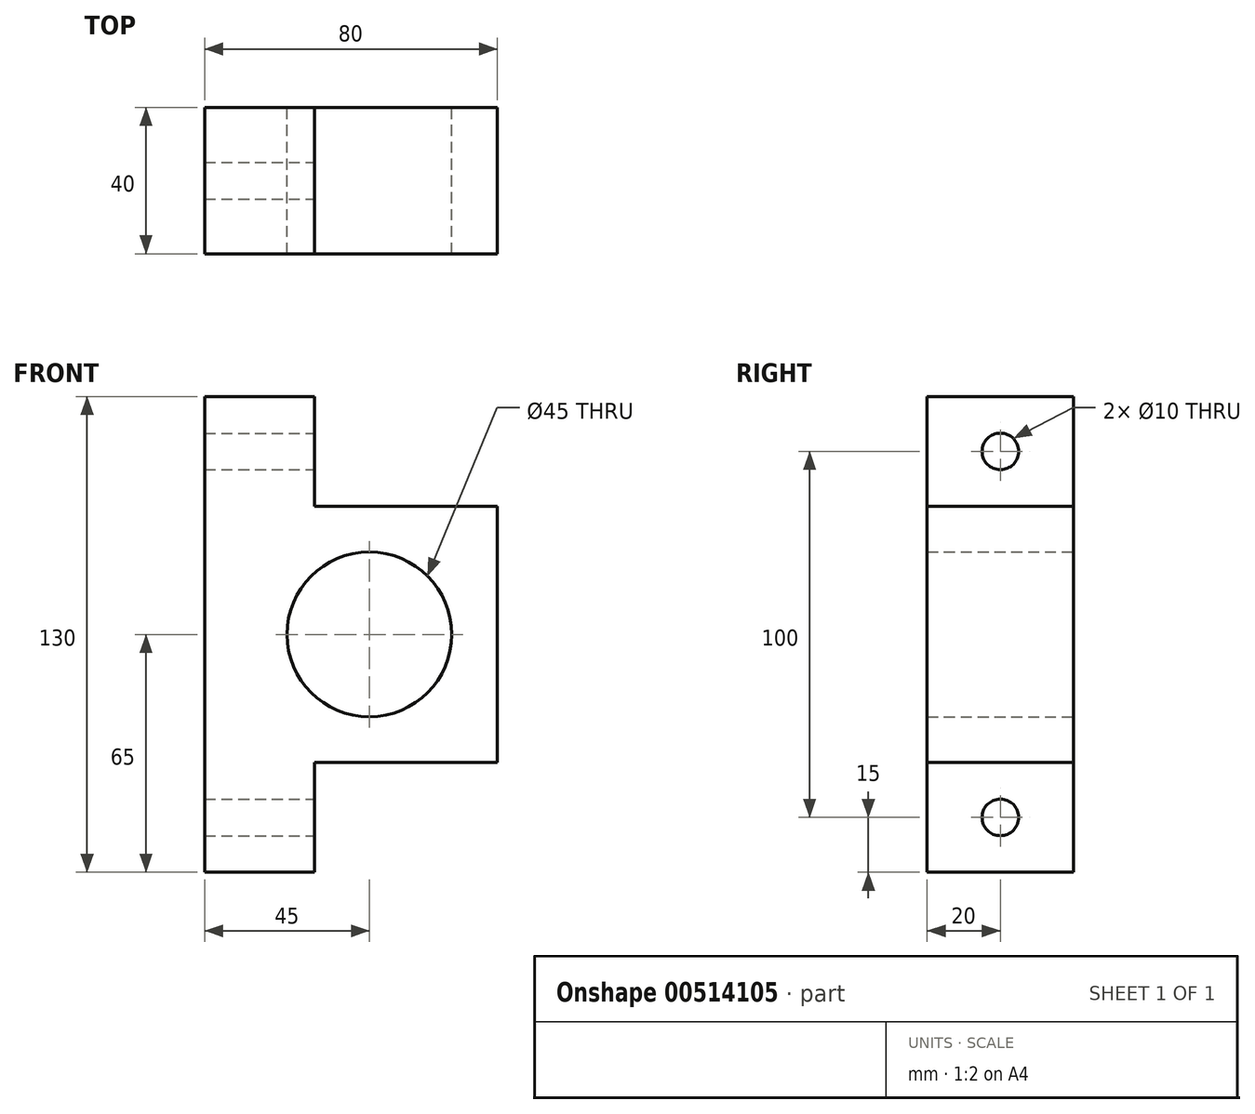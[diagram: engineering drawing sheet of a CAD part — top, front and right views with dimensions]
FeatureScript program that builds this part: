
annotation { "Feature Type Name" : "Feature", "Feature Type Description" : "" }
export const myFeature = defineFeature(function(context is Context, id is Id, definition is map)
    precondition{}
    {
        {
            var Q0;
            Q0=qCreatedBy(makeId("Front.planeOp"),FACE);
            var sketch = newSketch(context, id + "F0", { "sketchPlane" : qUnion([Q0])});
            skLineSegment(sketch, "E0", {"start": v(0, 0) * mm, "end": v(80, 0) * mm});
            skLineSegment(sketch, "E1", {"start": v(80, 0) * mm, "end": v(80, 70) * mm});
            skLineSegment(sketch, "E2", {"start": v(80, 70) * mm, "end": v(0, 70) * mm});
            skLineSegment(sketch, "E3", {"start": v(0, 70) * mm, "end": v(0, 0) * mm});
            skCircle(sketch, "E4", {"center": v(45, 35) * mm, "radius": 22.5 * mm});
            skLineSegment(sketch, "E5.bottom", {"start": v(0, 70) * mm, "end": v(30, 70) * mm});
            skLineSegment(sketch, "E5.top", {"start": v(0, 100) * mm, "end": v(30, 100) * mm});
            skLineSegment(sketch, "E5.left", {"start": v(0, 70) * mm, "end": v(0, 100) * mm});
            skLineSegment(sketch, "E5.right", {"start": v(30, 70) * mm, "end": v(30, 100) * mm});
            skLineSegment(sketch, "E6.bottom", {"start": v(0, 0) * mm, "end": v(30, 0) * mm});
            skLineSegment(sketch, "E6.top", {"start": v(0, -30) * mm, "end": v(30, -30) * mm});
            skLineSegment(sketch, "E6.left", {"start": v(0, 0) * mm, "end": v(0, -30) * mm});
            skLineSegment(sketch, "E6.right", {"start": v(30, 0) * mm, "end": v(30, -30) * mm});
            skSolve(sketch);
        }
        {
            var Q0;
            Q0 = qSketchRegion(id + "F0", true);
            extrude(context, id + "F1", {"entities" : qUnion([Q0]), "depth" : 40 * mm});
        }
        {
            var Q0;
            Q0=makeQuery(id+"F1.opExtrude","SWEPT_FACE",FACE,{"disambiguationData":[OSD([sQuery(id+"F0.wireOp",EDGE,"E5.right")])]});
            var sketch = newSketch(context, id + "F2", { "sketchPlane" : qUnion([Q0])});
            skCircle(sketch, "E7", {"center": v(-20, 85) * mm, "radius": 5 * mm});
            skCircle(sketch, "E8", {"center": v(-20, -15) * mm, "radius": 5 * mm});
            skSolve(sketch);
        }
        {
            var Q0;
            Q0 = qSketchRegion(id + "F2", true);
            extrude(context, id + "F3", {"entities" : qUnion([Q0]), "operationType" : NewBodyOperationType.REMOVE, "endBound" : BoundingType.THROUGH_ALL, "oppositeDirection" : true, "depth" : 25 * mm});
        }
    });
